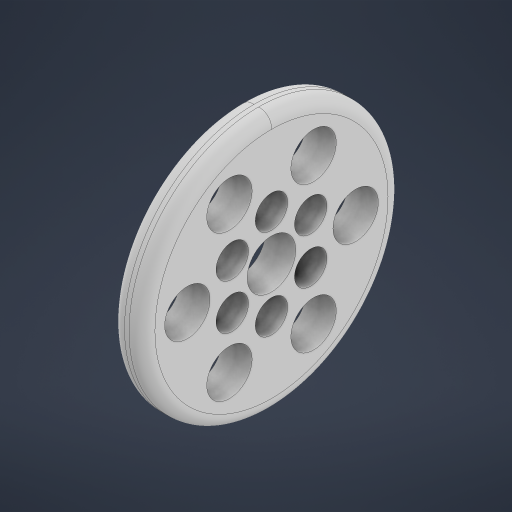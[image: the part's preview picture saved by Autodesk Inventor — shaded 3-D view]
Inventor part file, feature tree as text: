
AUTODESK INVENTOR PART (.ipt)
format: ipt  version: 2024.2 (Build 282272000, 272)  size: 642,560 bytes
history: native  units: in
note: dims shown in document units (in); Inventor stores cm internally (conversion verified against a paired STEP export)
features: extrude x2, sketch x2, fillet x1
ambient origin geometry x8: Origin, YZ Plane, XZ Plane, XY Plane, X Axis, Y Axis, Z Axis, Center Point
bodies: Solid1 (feature_tree)
feature tree (5):
  extrude  "Extrusion1"  Depth=0.185in
  fillet  "Fillet1"  Radius=0.185in
  extrude  "Extrusion2"  Depth=0.185in TaperAngle=360.0deg
  sketch  "Sketch2"  dims[d0=1.5748in d1=0.2953in d2=0.185in d3=0.0in]
  sketch  "Sketch3"  dims[d4=1.5748in d6=360.0deg d8=3.1496in d10=360.0deg d12=0.2953in d13=0.0787in d15=0.1969in d16=0.2756in d17=2.3622in d19=360.0deg d21=0.2756in d27=0.0in d28=0.5118in d31=2.3622in d33=360.0deg d35=0.185in d36=0.0in d37=0.0in d38=0.0in d39=0.0in d40=0.0in]
